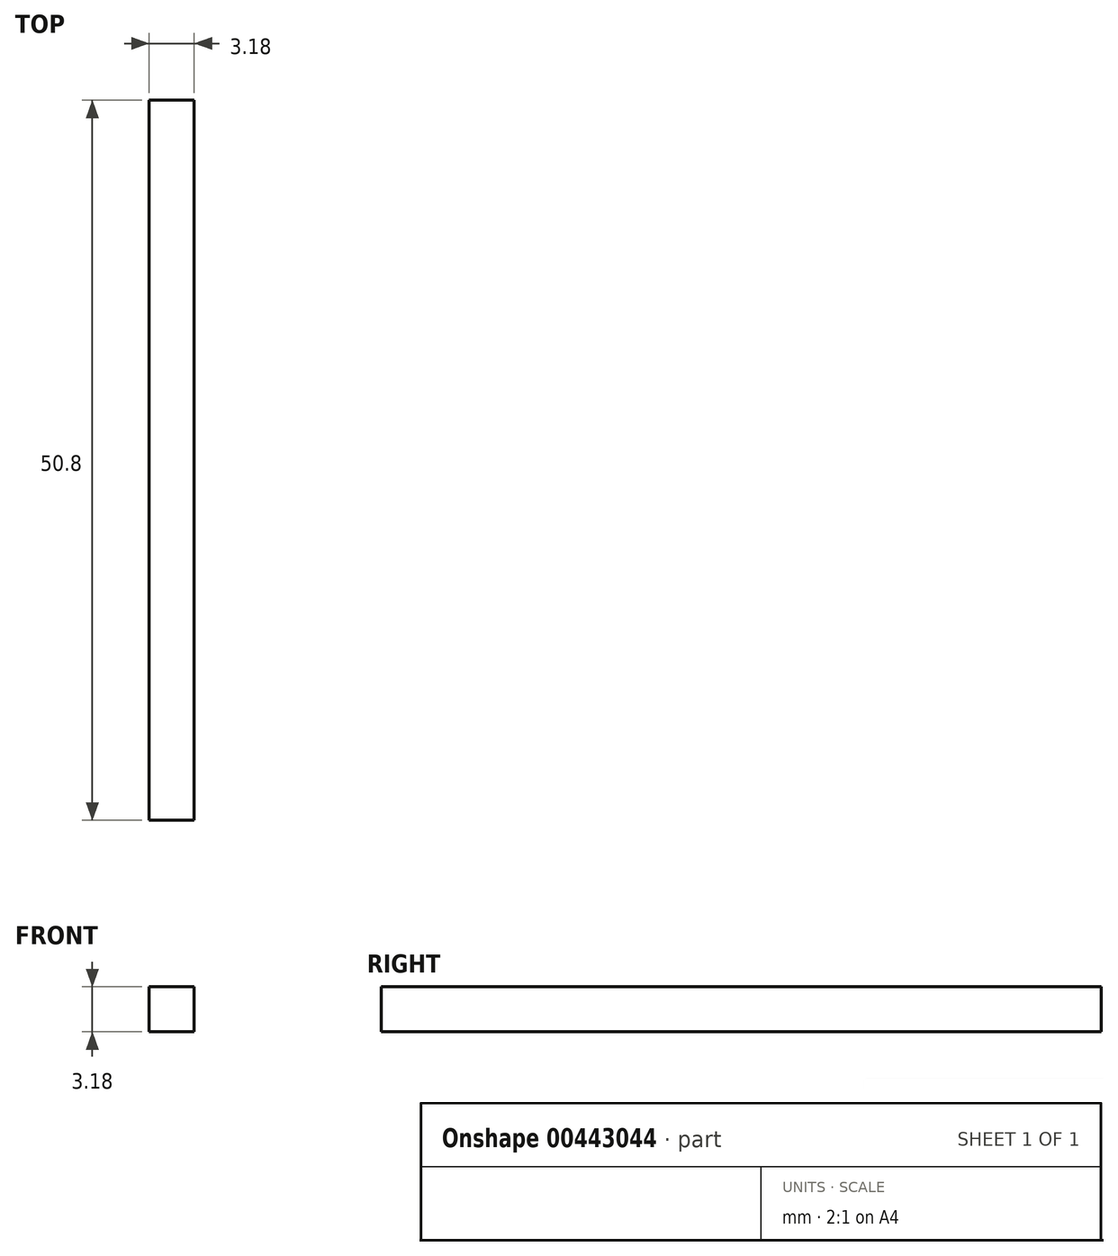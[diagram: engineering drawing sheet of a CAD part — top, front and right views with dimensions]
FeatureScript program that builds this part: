
annotation { "Feature Type Name" : "Feature", "Feature Type Description" : "" }
export const myFeature = defineFeature(function(context is Context, id is Id, definition is map)
    precondition{}
    {
        {
            var Q0;
            Q0=qCreatedBy(makeId("Front.planeOp"),FACE);
            var sketch = newSketch(context, id + "F0", { "sketchPlane" : qUnion([Q0])});
            skLineSegment(sketch, "E0.bottom", {"start": v(1.59, -1.59) * mm, "end": v(-1.59, -1.59) * mm});
            skLineSegment(sketch, "E0.top", {"start": v(1.59, 1.59) * mm, "end": v(-1.59, 1.59) * mm});
            skLineSegment(sketch, "E0.left", {"start": v(1.59, -1.59) * mm, "end": v(1.59, 1.59) * mm});
            skLineSegment(sketch, "E0.right", {"start": v(-1.59, -1.59) * mm, "end": v(-1.59, 1.59) * mm});
            skPoint(sketch, "E0.middle", {"position": v(0, 0) * mm});
            skSolve(sketch);
        }
        {
            var Q0;
            Q0=makeQuery(id+"F0.imprint","IMPRINT",FACE,{"disambiguationData":[TD([[makeQuery(id+"F0.imprint","IMPRINT",EDGE,{"derivedFrom":sQuery(id+"F0.wireOp",EDGE,"E0.bottom")}),-1.0]])]});
            extrude(context, id + "F1", {"entities" : qUnion([Q0]), "endBound" : BoundingType.SYMMETRIC, "depth" : 50.8 * mm});
        }
    });
